# Revit family: CV-CM
name_source: partatom
category: Lighting Fixtures
revit_build: Autodesk Revit 2014 (Build: 20130308_1515(x64)
units: mm (PartAtom-declared; Revit-internal decimal feet)

## types (6) — shared parameters
Color Filter = 16777215
Default Elevation = 48"
Description = Curv's narrow profile creates a sleek look that will enhance any building décor. Optional bull nose or shallow end caps offer alternative fixture appearances.
Dimming Lamp Color Temperature Shift = <None>
Emit Shape Visible in Rendering = No
Emit from Rectangle Length = 94"
Emit from Rectangle Width = 7"
Glass = Hubbell - White Glass
Housing Material = Hubbell - White
Lamp = T5, T5HO & T8
Load Classification = Lighting
Manufacturer = Alera Lighting
Model = CV
Photometric Notes = More IES files download on Photometric Web Link
Photometric Web Link = https://www.hubbell.com
Power Factor = 1
Product Documentation Link = https://hubbellcdn.com
Product Page URL = https://www.hubbell.com
Row Length = 96"
Suspension Height = 36"
Tilt Angle = -90.00°
URL = https://www.hubbell.com
Voltage = 120 V

## per-type parameters (varying)
| type | Apparent Load | Housing Type | Lamp Type | Photometric Web File | Watts |
| CV-1T5HO-PERF-CM-EP | 63 VA | CV-Housing : Perforated | One T5HO Lamps | CV-1T5HO-PERF-CM-EP.ies | 63 W |
| CV-1T5HO-S-EP | 61 VA | CV-Housing : Solid | One T5HO Lamps | CV-1T5HO-S-EP.ies | 61 W |
| CV-2T5HO-PERF-CM-EP | 118 VA | CV-Housing : Perforated | Two T5HO Lamps | CV-2T5HO-PERF-CM-EP.ies | 118 W |
| CV-2T5HO-S-EP | 118 VA | CV-Housing : Solid | Two T5HO Lamps | CV-2T5HO-S-EP.ies | 118 W |
| CV-3T5HO-PERF-CM-EP | 170 VA | CV-Housing : Perforated | Three T5HO Lamps | CV-3T5HO-PERF-CM-EP.ies | 170 W |
| CV-3T8-S-E | 88 VA | CV-Housing : Solid | Three T8 Lamps | CV-3T8-S-E.ies | 88 W |

## geometry (parser evidence)
native form markers: Blend x5, Sweep x3
no freeform markers — native parametric forms only
